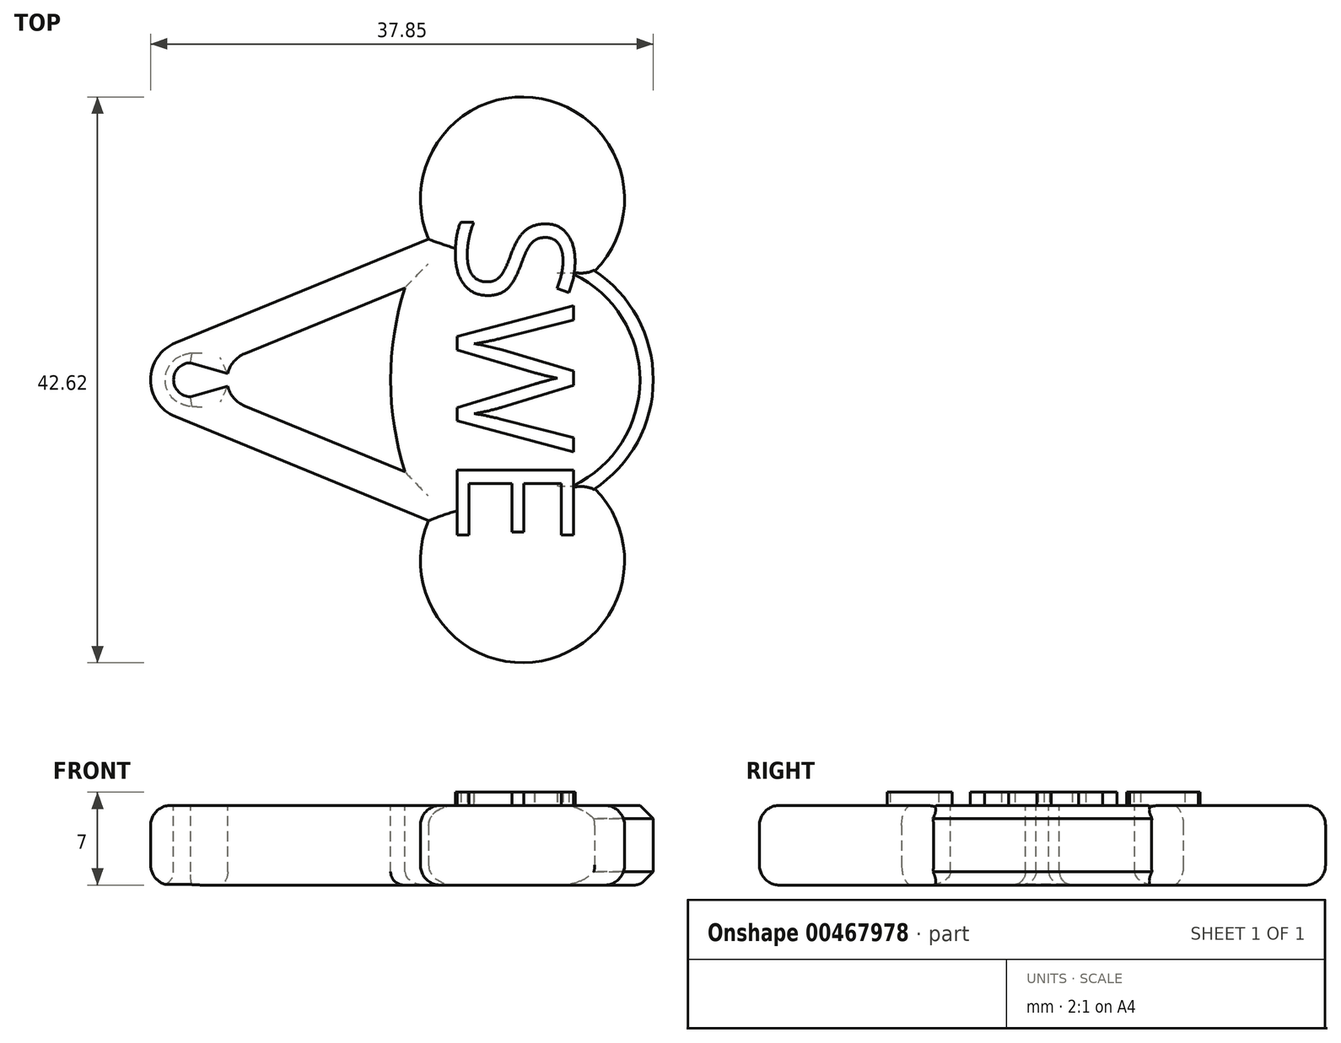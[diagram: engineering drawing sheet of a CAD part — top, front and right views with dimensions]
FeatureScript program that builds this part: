
annotation { "Feature Type Name" : "Feature", "Feature Type Description" : "" }
export const myFeature = defineFeature(function(context is Context, id is Id, definition is map)
    precondition{}
    {
        {
            var Q0;
            Q0=qCreatedBy(makeId("Top.planeOp"),FACE);
            var sketch = newSketch(context, id + "F0", { "sketchPlane" : qUnion([Q0])});
            skCircle(sketch, "E0", {"center": v(0, 0) * mm, "radius": 3 * mm});
            skLineSegment(sketch, "E1", {"start": v(-1.14, 2.77) * mm, "end": v(17.93, 10.6) * mm});
            skLineSegment(sketch, "E2", {"start": v(-1.14, -2.77) * mm, "end": v(17.93, -10.6) * mm});
            skArc(sketch, "E3", {"start": v(30.45, 8.2) * mm, "mid": v(26.45, 21.18) * mm, "end": v(17.93, 10.6) * mm});
            skPoint(sketch, "E4.orphan", {"position": v(20.25, 11.56) * mm});
            skArc(sketch, "E5", {"start": v(17.93, -10.6) * mm, "mid": v(26.45, -21.18) * mm, "end": v(30.45, -8.2) * mm});
            skArc(sketch, "E6.trimOffspring", {"start": v(30.45, -8.2) * mm, "mid": v(34.85, 0) * mm, "end": v(30.45, 8.2) * mm});
            skPoint(sketch, "E7.end.orphan", {"position": v(20.25, -11.56) * mm});
            skSolve(sketch);
        }
        {
            var Q0;
            Q0=qSketchRegion(id+"F0",true);
            extrude(context, id + "F1", {"entities" : qUnion([Q0]), "depth" : 3 * mm, "hasSecondDirection" : true, "secondDirectionOppositeDirection" : true, "secondDirectionDepth" : 3 * mm});
        }
        {
            var Q0;
            Q0=qCreatedBy(makeId("Top.planeOp"),FACE);
            var sketch = newSketch(context, id + "F2", { "sketchPlane" : qUnion([Q0])});
            skLineSegment(sketch, "E8", {"start": v(4.08, 1.97) * mm, "end": v(16.15, 6.93) * mm});
            skLineSegment(sketch, "E9", {"start": v(4.08, -1.97) * mm, "end": v(16.15, -6.93) * mm});
            skArc(sketch, "E10", {"start": v(4.08, 1.97) * mm, "mid": v(2.76, 0) * mm, "end": v(4.08, -1.97) * mm});
            skArc(sketch, "E11", {"start": v(16.15, 6.93) * mm, "mid": v(15.07, 0) * mm, "end": v(16.15, -6.93) * mm});
            skSolve(sketch);
        }
        {
            var Q0;
            Q0=qSketchRegion(id+"F2",true);
            var Q1;
            Q1=makeQuery(id+"F1.opExtrude","CAP_FACE",FACE,{"disambiguationData":[OSD([sQuery(id+"F0.wireOp",EDGE,"E0"),sQuery(id+"F0.wireOp",EDGE,"E7"),sQuery(id+"F0.wireOp",EDGE,"E1"),sQuery(id+"F0.wireOp",EDGE,"E2")])],"isStart":true});
            var Q2;
            Q2=makeQuery(id+"F1.opExtrude","CAP_FACE",FACE,{"disambiguationData":[OSD([sQuery(id+"F0.wireOp",EDGE,"E0"),sQuery(id+"F0.wireOp",EDGE,"E7"),sQuery(id+"F0.wireOp",EDGE,"E1"),sQuery(id+"F0.wireOp",EDGE,"E2")])],"isStart":false});
            extrude(context, id + "F3", {"entities" : qUnion([Q0]), "operationType" : NewBodyOperationType.REMOVE, "endBound" : BoundingType.UP_TO_SURFACE, "oppositeDirection" : true, "endBoundEntityFace" : qUnion([Q1]), "depth" : 25 * mm, "hasSecondDirection" : true, "secondDirectionBound" : SecondDirectionBoundingType.UP_TO_SURFACE, "secondDirectionOppositeDirection" : false, "secondDirectionBoundEntityFace" : qUnion([Q2]), "secondDirectionDepth" : 25 * mm});
        }
        {
            var Q0;
            Q0=makeQuery(id+"F1.opExtrude","CAP_FACE",FACE,{"disambiguationData":[OSD([sQuery(id+"F0.wireOp",EDGE,"E0"),sQuery(id+"F0.wireOp",EDGE,"E7"),sQuery(id+"F0.wireOp",EDGE,"E1"),sQuery(id+"F0.wireOp",EDGE,"E2")])],"isStart":false});
            var sketch = newSketch(context, id + "F4", { "sketchPlane" : qUnion([Q0])});
            skArc(sketch, "E12", {"start": v(0, 1.27) * mm, "mid": v(-1.27, 0) * mm, "end": v(0, -1.27) * mm});
            skLineSegment(sketch, "E13", {"start": v(0, -1.27) * mm, "end": v(4.5, 0) * mm});
            skLineSegment(sketch, "E14", {"start": v(4.5, 0) * mm, "end": v(0, 1.28) * mm});
            skLineSegment(sketch, "E15", {"start": v(0, -3.24) * mm, "end": v(0, 3.24) * mm, "construction": true});
            skSolve(sketch);
        }
        {
            var Q0;
            Q0=qSketchRegion(id+"F4",true);
            var Q1;
            Q1=makeQuery(id+"F1.opExtrude","CAP_FACE",FACE,{"disambiguationData":[OSD([sQuery(id+"F0.wireOp",EDGE,"E0"),sQuery(id+"F0.wireOp",EDGE,"E7"),sQuery(id+"F0.wireOp",EDGE,"E1"),sQuery(id+"F0.wireOp",EDGE,"E2")])],"isStart":true});
            extrude(context, id + "F5", {"entities" : qUnion([Q0]), "operationType" : NewBodyOperationType.REMOVE, "endBound" : BoundingType.UP_TO_SURFACE, "oppositeDirection" : true, "endBoundEntityFace" : qUnion([Q1]), "depth" : 25 * mm});
        }
        {
            var Q0;
            Q0=makeQuery(id+"F1.opExtrude","CAP_FACE",FACE,{"disambiguationData":[OSD([sQuery(id+"F0.wireOp",EDGE,"E0"),sQuery(id+"F0.wireOp",EDGE,"E7"),sQuery(id+"F0.wireOp",EDGE,"E1"),sQuery(id+"F0.wireOp",EDGE,"E2")])],"isStart":false});
            var sketch = newSketch(context, id + "F6", { "sketchPlane" : qUnion([Q0])});
            skText(sketch, "E16", { "text": "SWE", "fontName": "OpenSans-Regular.ttf"});
            const initialGuessF6  = {"E16": [0.02007, 0.0125, 0, -1, 0.00884]};
            skSetInitialGuess(sketch, initialGuessF6);
            skSolve(sketch);
        }
        {
            var Q0;
            Q0=qSketchRegion(id+"F6",true);
            extrude(context, id + "F7", {"entities" : qUnion([Q0]), "operationType" : NewBodyOperationType.ADD, "depth" : 1 * mm});
        }
        {
            var Q0;
            Q0=makeQuery(id+"F1.opExtrude","CAP_EDGE",EDGE,{"disambiguationData":[OSD([sQuery(id+"F0.wireOp",EDGE,"E3")])],"isStart":false});
            var Q1;
            Q1=makeQuery(id+"F1.opExtrude","CAP_EDGE",EDGE,{"disambiguationData":[OSD([sQuery(id+"F0.wireOp",EDGE,"E5")])],"isStart":false});
            var Q2;
            Q2=makeQuery(id+"F1.opExtrude","CAP_EDGE",EDGE,{"disambiguationData":[OSD([sQuery(id+"F0.wireOp",EDGE,"E5")])],"isStart":true});
            var Q3;
            Q3=makeQuery(id+"F1.opExtrude","CAP_EDGE",EDGE,{"disambiguationData":[OSD([sQuery(id+"F0.wireOp",EDGE,"E3")])],"isStart":true});
            var Q4;
            Q4=makeQuery(id+"F1.opExtrude","CAP_EDGE",EDGE,{"disambiguationData":[OSD([sQuery(id+"F0.wireOp",EDGE,"E2")])],"isStart":false});
            var Q5;
            Q5=makeQuery(id+"F3.boolean.opBoolean","COPY",EDGE,{"derivedFrom":makeQuery(id+"F3.opExtrude","CAP_EDGE",EDGE,{"disambiguationData":[OSD([sQuery(id+"F2.wireOp",EDGE,"E11")])],"isStart":true})});
            var Q6;
            Q6=makeQuery(id+"F1.opExtrude","CAP_EDGE",EDGE,{"disambiguationData":[OSD([sQuery(id+"F0.wireOp",EDGE,"E2")])],"isStart":true});
            var Q7;
            Q7=makeQuery(id+"F3.boolean.opBoolean","COPY",EDGE,{"derivedFrom":makeQuery(id+"F3.opExtrude","CAP_EDGE",EDGE,{"disambiguationData":[OSD([sQuery(id+"F2.wireOp",EDGE,"E9")])],"isStart":false})});
            var Q8;
            Q8=makeQuery(id+"F3.boolean.opBoolean","COPY",EDGE,{"derivedFrom":makeQuery(id+"F3.opExtrude","CAP_EDGE",EDGE,{"disambiguationData":[OSD([sQuery(id+"F2.wireOp",EDGE,"E8")])],"isStart":false})});
            var Q9;
            Q9=makeQuery(id+"F3.boolean.opBoolean","COPY",EDGE,{"derivedFrom":makeQuery(id+"F3.opExtrude","CAP_EDGE",EDGE,{"disambiguationData":[OSD([sQuery(id+"F2.wireOp",EDGE,"E11")])],"isStart":false})});
            fillet(context, id + "F8", {"entities" : qUnion([Q0, Q1, Q2, Q3, Q4, Q5, Q6, Q7, Q8, Q9]), "radius" : 1.5 * mm, "tangentPropagation" : true, "allowEdgeOverflow" : false});
        }
        {
            var Q0;
            Q0=makeQuery(id+"F1.opExtrude","CAP_EDGE",EDGE,{"disambiguationData":[OSD([sQuery(id+"F0.wireOp",EDGE,"E6.trimOffspring")])],"isStart":false});
            var Q1;
            Q1=makeQuery(id+"F1.opExtrude","CAP_EDGE",EDGE,{"disambiguationData":[OSD([sQuery(id+"F0.wireOp",EDGE,"E6.trimOffspring")])],"isStart":true});
            chamfer(context, id + "F9", {"entities" : qUnion([Q0, Q1]), "width" : 1 * mm, "tangentPropagation" : true});
        }
        {
            var Q0;
            Q0=makeQuery(id+"F5.boolean.opBoolean","COPY",EDGE,{"derivedFrom":makeQuery(id+"F5.opExtrude","CAP_EDGE",EDGE,{"disambiguationData":[OSD([sQuery(id+"F4.wireOp",EDGE,"E12")])],"isStart":true})});
            var Q1;
            Q1=makeQuery(id+"F5.boolean.opBoolean","COPY",EDGE,{"derivedFrom":makeQuery(id+"F5.opExtrude","CAP_EDGE",EDGE,{"disambiguationData":[OSD([sQuery(id+"F4.wireOp",EDGE,"E13")])],"isStart":true})});
            var Q2;
            Q2=makeQuery(id+"F5.boolean.opBoolean","COPY",EDGE,{"derivedFrom":makeQuery(id+"F5.opExtrude","CAP_EDGE",EDGE,{"disambiguationData":[OSD([sQuery(id+"F4.wireOp",EDGE,"E14")])],"isStart":true})});
            var Q3;
            Q3=makeQuery(id+"F5.boolean.opBoolean","COPY",EDGE,{"derivedFrom":makeQuery(id+"F5.opExtrude","CAP_EDGE",EDGE,{"disambiguationData":[OSD([sQuery(id+"F4.wireOp",EDGE,"E12")])],"isStart":false})});
            var Q4;
            Q4=makeQuery(id+"F5.boolean.opBoolean","COPY",EDGE,{"derivedFrom":makeQuery(id+"F5.opExtrude","CAP_EDGE",EDGE,{"disambiguationData":[OSD([sQuery(id+"F4.wireOp",EDGE,"E14")])],"isStart":false})});
            var Q5;
            Q5=makeQuery(id+"F8.opFillet","SPLIT",FACE,{"disambiguationData":[OD(0.0)],"derivedFrom":makeQuery(id+"F1.opExtrude","CAP_FACE",FACE,{"disambiguationData":[OSD([sQuery(id+"F0.wireOp",EDGE,"E0"),sQuery(id+"F0.wireOp",EDGE,"E1"),sQuery(id+"F0.wireOp",EDGE,"E2"),sQuery(id+"F0.wireOp",EDGE,"E3"),sQuery(id+"F0.wireOp",EDGE,"E5"),sQuery(id+"F0.wireOp",EDGE,"E6.trimOffspring")])],"isStart":true})});
            fillet(context, id + "F10", {"entities" : qUnion([Q0, Q1, Q2, Q3, Q4, Q5]), "radius" : 1 * mm, "tangentPropagation" : true, "allowEdgeOverflow" : false});
        }
    });
